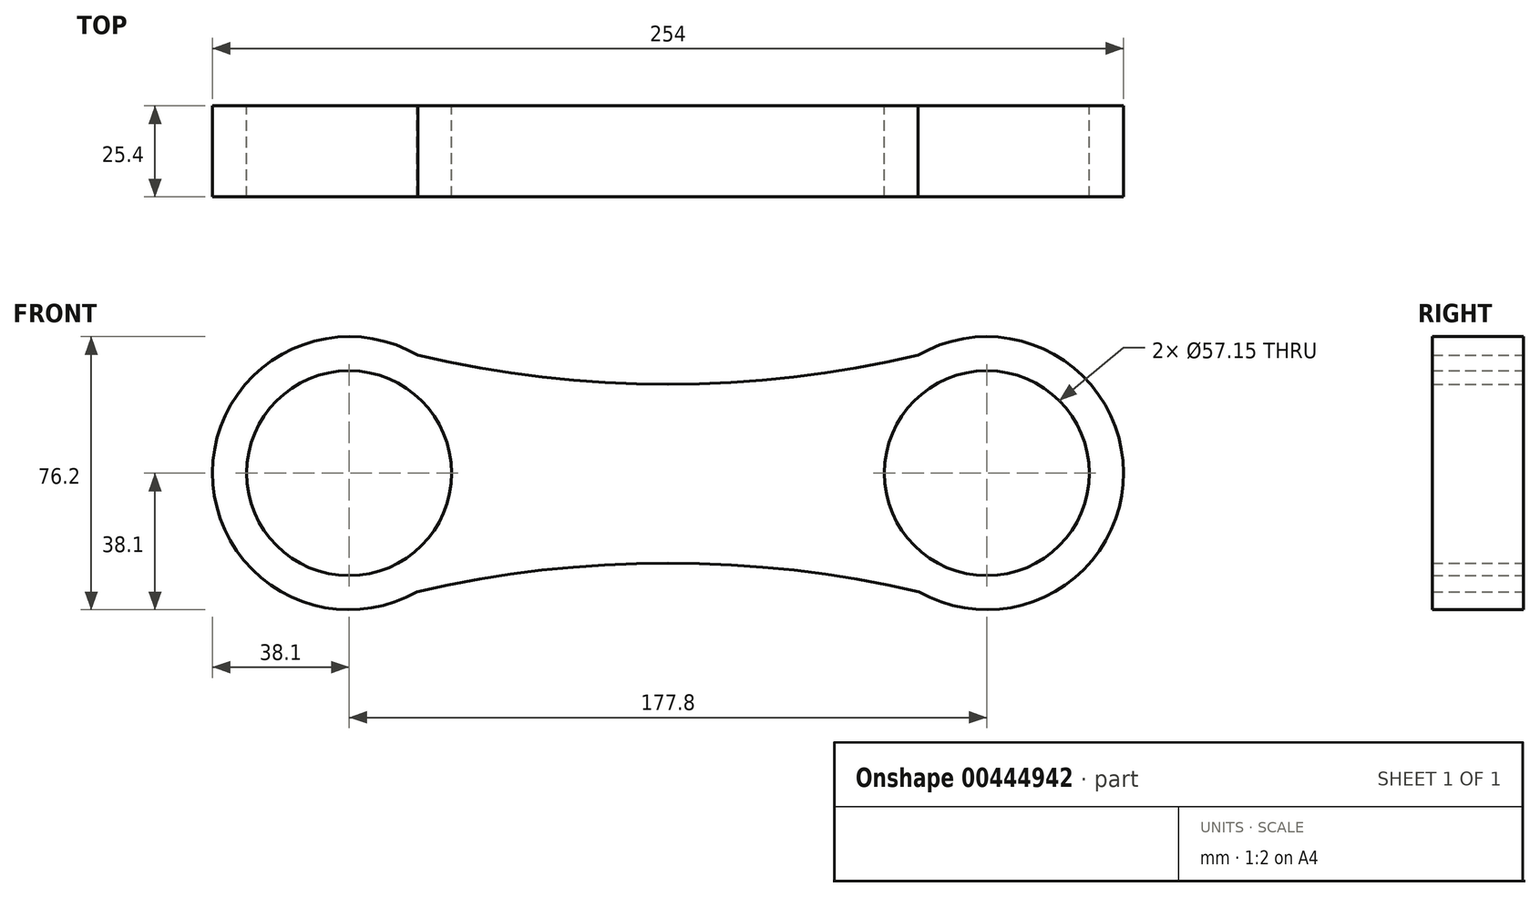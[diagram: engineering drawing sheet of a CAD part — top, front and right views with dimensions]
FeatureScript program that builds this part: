
annotation { "Feature Type Name" : "Feature", "Feature Type Description" : "" }
export const myFeature = defineFeature(function(context is Context, id is Id, definition is map)
    precondition{}
    {
        {
            var Q0;
            Q0=qCreatedBy(makeId("Front.planeOp"),FACE);
            var sketch = newSketch(context, id + "F0", { "sketchPlane" : qUnion([Q0])});
            skCircle(sketch, "E0", {"center": v(-88.9, 0) * mm, "radius": 38.1 * mm});
            skCircle(sketch, "E1", {"center": v(88.9, 0) * mm, "radius": 38.1 * mm});
            skArc(sketch, "E2", {"start": v(-88.9, 38.1) * mm, "mid": v(0, 24.78) * mm, "end": v(88.9, 38.1) * mm});
            skArc(sketch, "E3", {"start": v(88.9, -38.1) * mm, "mid": v(0, -25.06) * mm, "end": v(-88.9, -38.1) * mm});
            skCircle(sketch, "E4", {"center": v(-88.9, 0) * mm, "radius": 28.58 * mm});
            skCircle(sketch, "E5", {"center": v(88.9, 0) * mm, "radius": 28.58 * mm});
            skSolve(sketch);
        }
        {
            var Q0;
            Q0 = qSketchRegion(id + "F0", true);
            extrude(context, id + "F1", {"entities" : qUnion([Q0]), "depth" : 25.4 * mm});
        }
    });
